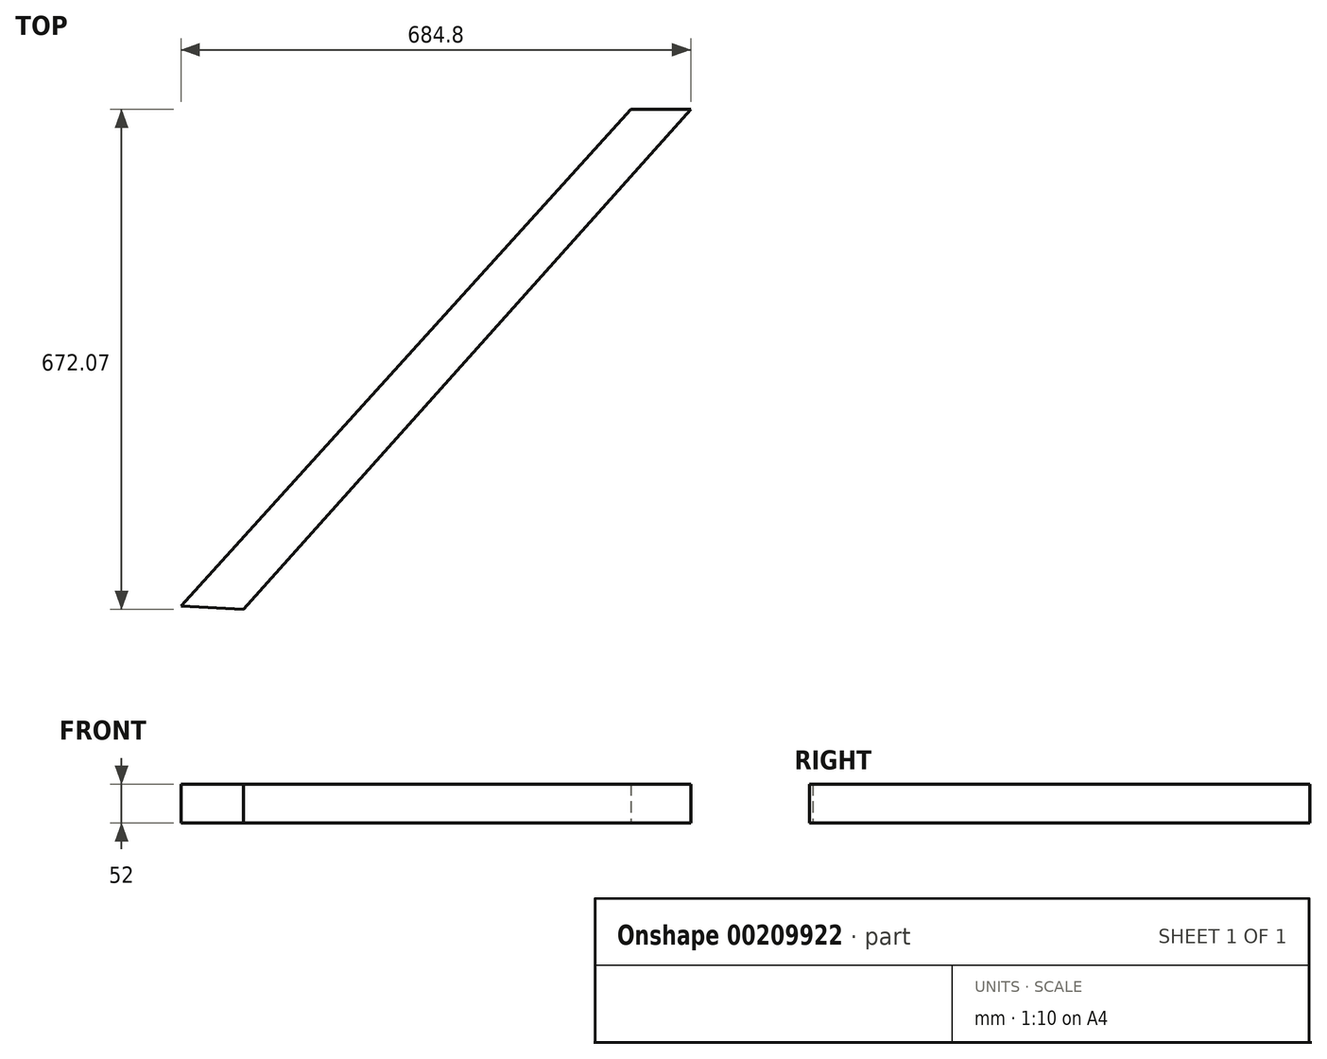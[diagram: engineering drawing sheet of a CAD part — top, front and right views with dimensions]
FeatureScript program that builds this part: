
annotation { "Feature Type Name" : "Feature", "Feature Type Description" : "" }
export const myFeature = defineFeature(function(context is Context, id is Id, definition is map)
    precondition{}
    {
        {
            var Q0;
            Q0=qCreatedBy(makeId("Top.planeOp"),FACE);
            var sketch = newSketch(context, id + "F0", { "sketchPlane" : qUnion([Q0])});
            skLineSegment(sketch, "E0", {"start": v(-792.05, -322.81) * mm, "end": v(-187.9, 345.01) * mm});
            skLineSegment(sketch, "E1", {"start": v(-187.9, 345.01) * mm, "end": v(-107.25, 345.01) * mm});
            skLineSegment(sketch, "E2", {"start": v(-107.25, 345.01) * mm, "end": v(-708.57, -327.06) * mm});
            skLineSegment(sketch, "E3", {"start": v(-708.57, -327.06) * mm, "end": v(-792.05, -322.81) * mm});
            skSolve(sketch);
        }
        {
            var Q0;
            Q0 = qSketchRegion(id + "F0", true);
            extrude(context, id + "F1", {"entities" : qUnion([Q0]), "depth" : 52 * mm});
        }
    });
